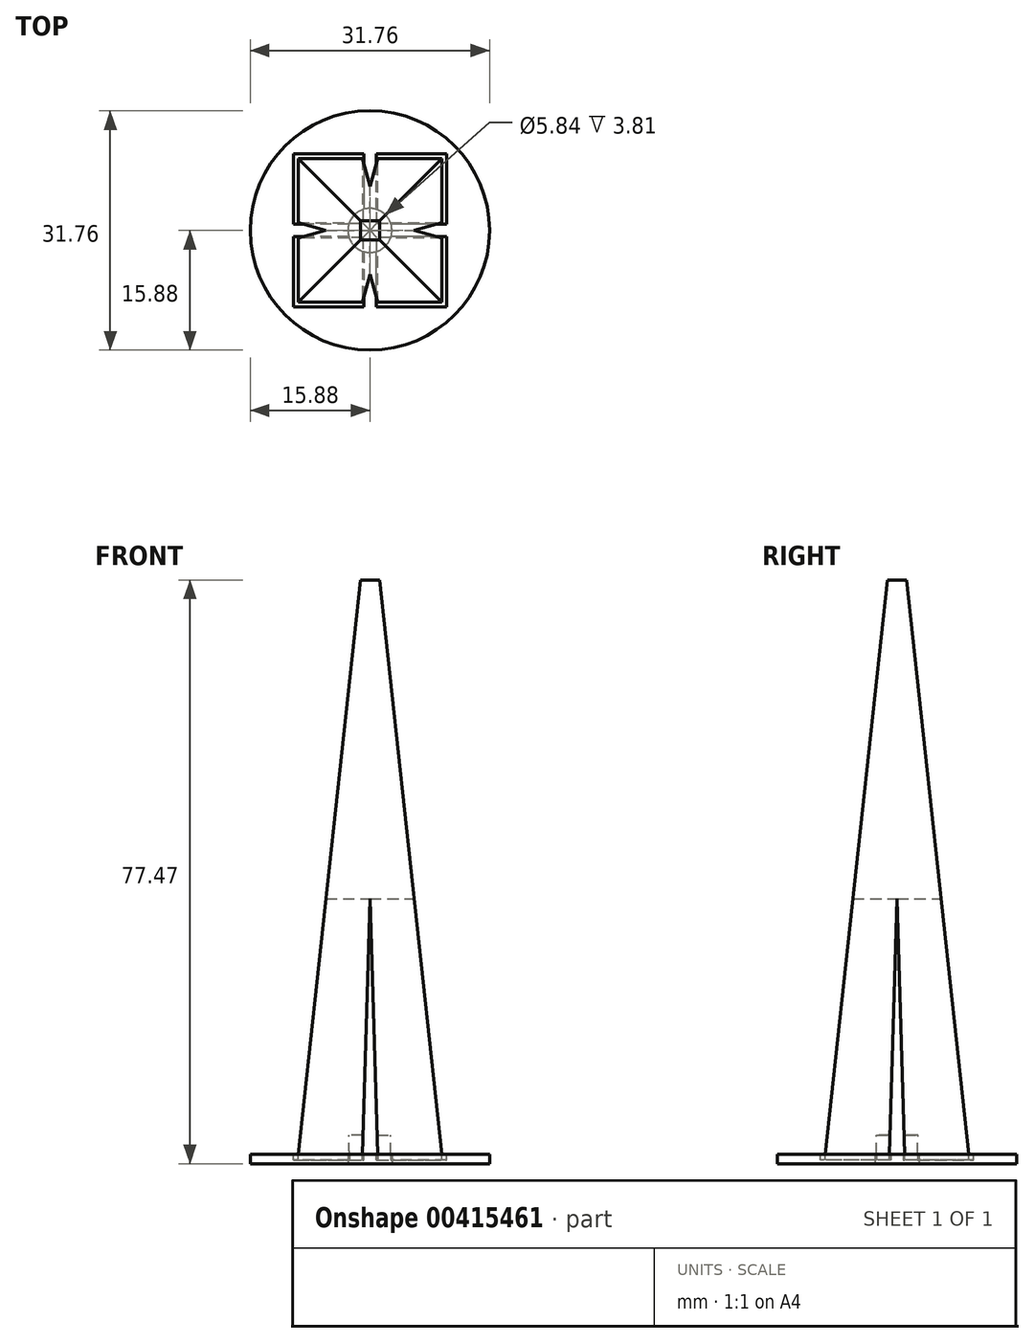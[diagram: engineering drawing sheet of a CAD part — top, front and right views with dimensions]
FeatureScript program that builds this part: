
annotation { "Feature Type Name" : "Feature", "Feature Type Description" : "" }
export const myFeature = defineFeature(function(context is Context, id is Id, definition is map)
    precondition{}
    {
        {
            var Q0;
            Q0=qCreatedBy(makeId("Top.planeOp"),FACE);
            var sketch = newSketch(context, id + "F0", { "sketchPlane" : qUnion([Q0])});
            skCircle(sketch, "E0", {"center": v(0, 0) * mm, "radius": 15.88 * mm});
            skSolve(sketch);
        }
        {
            var Q0;
            Q0=makeQuery(id+"F0.imprint","IMPRINT",FACE,{"disambiguationData":[TD([[makeQuery(id+"F0.imprint","IMPRINT",EDGE,{"derivedFrom":sQuery(id+"F0.wireOp",EDGE,"E0")}),1.0]])]});
            extrude(context, id + "F1", {"entities" : qUnion([Q0]), "oppositeDirection" : true, "depth" : 1.27 * mm});
        }
        {
            var Q0;
            Q0=qCreatedBy(makeId("Top.planeOp"),FACE);
            var sketch = newSketch(context, id + "F2", { "sketchPlane" : qUnion([Q0])});
            skLineSegment(sketch, "E1.bottom", {"start": v(-9.52, 9.53) * mm, "end": v(9.53, 9.53) * mm});
            skLineSegment(sketch, "E1.top", {"start": v(-9.53, -9.53) * mm, "end": v(9.52, -9.53) * mm});
            skLineSegment(sketch, "E1.left", {"start": v(-9.52, 9.53) * mm, "end": v(-9.53, -9.53) * mm});
            skLineSegment(sketch, "E1.right", {"start": v(9.53, 9.53) * mm, "end": v(9.52, -9.53) * mm});
            skPoint(sketch, "E1.middle", {"position": v(0, 0) * mm});
            skLineSegment(sketch, "E2", {"start": v(-1.02, 9.52) * mm, "end": v(-1.02, -9.52) * mm});
            skLineSegment(sketch, "E3", {"start": v(1.02, -9.52) * mm, "end": v(1.02, 9.52) * mm});
            skLineSegment(sketch, "E4", {"start": v(-9.52, 1.02) * mm, "end": v(9.53, 1.02) * mm});
            skLineSegment(sketch, "E5", {"start": v(9.53, -1.02) * mm, "end": v(-9.52, -1.02) * mm});
            skLineSegment(sketch, "E6", {"start": v(0, 9.53) * mm, "end": v(0, 0) * mm, "construction": true});
            skLineSegment(sketch, "E7", {"start": v(0, 0) * mm, "end": v(0, -9.53) * mm, "construction": true});
            skLineSegment(sketch, "E8", {"start": v(0, 0) * mm, "end": v(9.53, 0) * mm, "construction": true});
            skLineSegment(sketch, "E9", {"start": v(0, 0) * mm, "end": v(-9.53, 0) * mm, "construction": true});
            skSolve(sketch);
        }
        {
            var Q0;
            Q0=qCreatedBy(makeId("Top.planeOp"),FACE);
            cPlane(context, id + "F3", {"entities" : qUnion([Q0]), "cplaneType" : CPlaneType.OFFSET, "offset" : 76.2 * mm, "width" : 152.4 * mm, "height" : 152.4 * mm});
        }
        {
            var Q0;
            Q0=qCreatedBy(id+"F3.planeOp",FACE);
            var sketch = newSketch(context, id + "F4", { "sketchPlane" : qUnion([Q0])});
            skLineSegment(sketch, "E10.bottom", {"start": v(-1.27, 1.27) * mm, "end": v(1.27, 1.27) * mm});
            skLineSegment(sketch, "E10.top", {"start": v(-1.27, -1.27) * mm, "end": v(1.27, -1.27) * mm});
            skLineSegment(sketch, "E10.left", {"start": v(-1.27, 1.27) * mm, "end": v(-1.27, -1.27) * mm});
            skLineSegment(sketch, "E10.right", {"start": v(1.27, 1.27) * mm, "end": v(1.27, -1.27) * mm});
            skPoint(sketch, "E10.middle", {"position": v(0, 0) * mm});
            skSolve(sketch);
        }
        {
            var Q1;
            {var subQ0=sQuery(id+"F2.wireOp",EDGE,"E1.left");var subQ1=sQuery(id+"F2.wireOp",EDGE,"E1.bottom");var subQ2=makeQuery(id+"F2.imprint","INTERSECT",VERTEX,{"derivedFrom":[subQ1,subQ0]});Q1=makeQuery(id+"F2.imprint","IMPRINT",FACE,{"disambiguationData":[TD([[makeQuery(id+"F2.imprint","IMPRINT",EDGE,{"disambiguationData":[TD([[subQ2,-1.0]])],"derivedFrom":subQ1}),-1.0]])]});}
            var Q2;
            Q2=makeQuery(id+"F4.imprint","IMPRINT",FACE,{"disambiguationData":[TD([[makeQuery(id+"F4.imprint","IMPRINT",EDGE,{"derivedFrom":sQuery(id+"F4.wireOp",EDGE,"E10.bottom")}),-1.0]])]});
            loft(context, id + "F5", {"sheetProfilesArray" : [{ "sheetProfileEntities" : qUnion([Q1]) }, { "sheetProfileEntities" : qUnion([Q2]) }]});
        }
        {
            var Q1;
            {var subQ0=sQuery(id+"F2.wireOp",EDGE,"E1.right");var subQ1=sQuery(id+"F2.wireOp",EDGE,"E1.bottom");var subQ2=makeQuery(id+"F2.imprint","INTERSECT",VERTEX,{"derivedFrom":[subQ1,subQ0]});Q1=makeQuery(id+"F2.imprint","IMPRINT",FACE,{"disambiguationData":[TD([[makeQuery(id+"F2.imprint","IMPRINT",EDGE,{"disambiguationData":[TD([[subQ2,1.0]])],"derivedFrom":subQ1}),-1.0]])]});}
            var Q2;
            Q2=makeQuery(id+"F5.opLoft","CAP_FACE",FACE,{"disambiguationData":[OSD([makeQuery(id+"F4.imprint","IMPRINT",FACE,{"disambiguationData":[TD([[makeQuery(id+"F4.imprint","IMPRINT",EDGE,{"derivedFrom":sQuery(id+"F4.wireOp",EDGE,"E10.bottom")}),-1.0]])]})])],"isStart":true});
            loft(context, id + "F6", {"operationType" : NewBodyOperationType.ADD, "sheetProfilesArray" : [{ "sheetProfileEntities" : qUnion([Q1]) }, { "sheetProfileEntities" : qUnion([Q2]) }]});
        }
        {
            var Q1;
            {var subQ0=sQuery(id+"F2.wireOp",EDGE,"E1.left");var subQ1=sQuery(id+"F2.wireOp",EDGE,"E1.top");var subQ2=makeQuery(id+"F2.imprint","INTERSECT",VERTEX,{"derivedFrom":[subQ1,subQ0]});Q1=makeQuery(id+"F2.imprint","IMPRINT",FACE,{"disambiguationData":[TD([[makeQuery(id+"F2.imprint","IMPRINT",EDGE,{"disambiguationData":[TD([[subQ2,-1.0]])],"derivedFrom":subQ1}),1.0]])]});}
            var Q2;
            Q2=makeQuery(id+"F5.opLoft","CAP_FACE",FACE,{"disambiguationData":[OSD([makeQuery(id+"F4.imprint","IMPRINT",FACE,{"disambiguationData":[TD([[makeQuery(id+"F4.imprint","IMPRINT",EDGE,{"derivedFrom":sQuery(id+"F4.wireOp",EDGE,"E10.bottom")}),-1.0]])]})])],"isStart":true});
            loft(context, id + "F7", {"operationType" : NewBodyOperationType.ADD, "sheetProfilesArray" : [{ "sheetProfileEntities" : qUnion([Q1]) }, { "sheetProfileEntities" : qUnion([Q2]) }]});
        }
        {
            var Q1;
            {var subQ0=sQuery(id+"F2.wireOp",EDGE,"E1.right");var subQ1=sQuery(id+"F2.wireOp",EDGE,"E1.top");var subQ2=makeQuery(id+"F2.imprint","INTERSECT",VERTEX,{"derivedFrom":[subQ1,subQ0]});Q1=makeQuery(id+"F2.imprint","IMPRINT",FACE,{"disambiguationData":[TD([[makeQuery(id+"F2.imprint","IMPRINT",EDGE,{"disambiguationData":[TD([[subQ2,1.0]])],"derivedFrom":subQ1}),1.0]])]});}
            var Q2;
            Q2=makeQuery(id+"F5.opLoft","CAP_FACE",FACE,{"disambiguationData":[OSD([makeQuery(id+"F4.imprint","IMPRINT",FACE,{"disambiguationData":[TD([[makeQuery(id+"F4.imprint","IMPRINT",EDGE,{"derivedFrom":sQuery(id+"F4.wireOp",EDGE,"E10.bottom")}),-1.0]])]})])],"isStart":true});
            loft(context, id + "F8", {"operationType" : NewBodyOperationType.ADD, "sheetProfilesArray" : [{ "sheetProfileEntities" : qUnion([Q1]) }, { "sheetProfileEntities" : qUnion([Q2]) }]});
        }
        {
            var Q0;
            Q0=makeQuery(id+"F1.opExtrude","CAP_FACE",FACE,{"disambiguationData":[OSD([sQuery(id+"F0.wireOp",EDGE,"E0")])],"isStart":true});
            var sketch = newSketch(context, id + "F9", { "sketchPlane" : qUnion([Q0])});
            skLineSegment(sketch, "E11", {"start": v(0, 0) * mm, "end": v(0, 15.88) * mm, "construction": true});
            skLineSegment(sketch, "E12", {"start": v(0, 0) * mm, "end": v(15.88, 0) * mm, "construction": true});
            skLineSegment(sketch, "E13.bottom", {"start": v(-10.16, 10.16) * mm, "end": v(10.16, 10.16) * mm});
            skLineSegment(sketch, "E13.top", {"start": v(-10.16, -10.16) * mm, "end": v(10.16, -10.16) * mm});
            skLineSegment(sketch, "E13.left", {"start": v(-10.16, 10.16) * mm, "end": v(-10.16, -10.16) * mm});
            skLineSegment(sketch, "E13.right", {"start": v(10.16, 10.16) * mm, "end": v(10.16, -10.16) * mm});
            skPoint(sketch, "E13.middle", {"position": v(0, 0) * mm});
            skLineSegment(sketch, "E14", {"start": v(-0.83, 15.85) * mm, "end": v(-0.83, -15.85) * mm});
            skLineSegment(sketch, "E15", {"start": v(0.83, -15.85) * mm, "end": v(0.83, 15.85) * mm});
            skLineSegment(sketch, "E16", {"start": v(15.85, 0.83) * mm, "end": v(-15.85, 0.83) * mm});
            skLineSegment(sketch, "E17", {"start": v(15.85, -0.83) * mm, "end": v(-15.85, -0.83) * mm});
            skSolve(sketch);
        }
        {
            var Q0;
            {var subQ0=sQuery(id+"F9.wireOp",EDGE,"E13.right");var subQ1=sQuery(id+"F9.wireOp",EDGE,"E13.bottom");var subQ2=makeQuery(id+"F9.imprint","INTERSECT",VERTEX,{"derivedFrom":[subQ1,subQ0]});Q0=makeQuery(id+"F9.imprint","IMPRINT",FACE,{"disambiguationData":[TD([[makeQuery(id+"F9.imprint","IMPRINT",EDGE,{"disambiguationData":[TD([[subQ2,1.0]])],"derivedFrom":subQ1}),-1.0]])]});}
            var Q1;
            {var subQ0=sQuery(id+"F9.wireOp",EDGE,"E13.left");var subQ1=sQuery(id+"F9.wireOp",EDGE,"E13.bottom");var subQ2=makeQuery(id+"F9.imprint","INTERSECT",VERTEX,{"derivedFrom":[subQ1,subQ0]});Q1=makeQuery(id+"F9.imprint","IMPRINT",FACE,{"disambiguationData":[TD([[makeQuery(id+"F9.imprint","IMPRINT",EDGE,{"disambiguationData":[TD([[subQ2,-1.0]])],"derivedFrom":subQ1}),-1.0]])]});}
            var Q2;
            {var subQ0=sQuery(id+"F9.wireOp",EDGE,"E13.right");var subQ1=sQuery(id+"F9.wireOp",EDGE,"E13.top");var subQ2=makeQuery(id+"F9.imprint","INTERSECT",VERTEX,{"derivedFrom":[subQ1,subQ0]});Q2=makeQuery(id+"F9.imprint","IMPRINT",FACE,{"disambiguationData":[TD([[makeQuery(id+"F9.imprint","IMPRINT",EDGE,{"disambiguationData":[TD([[subQ2,1.0]])],"derivedFrom":subQ1}),1.0]])]});}
            var Q3;
            {var subQ0=sQuery(id+"F9.wireOp",EDGE,"E13.left");var subQ1=sQuery(id+"F9.wireOp",EDGE,"E13.top");var subQ2=makeQuery(id+"F9.imprint","INTERSECT",VERTEX,{"derivedFrom":[subQ1,subQ0]});Q3=makeQuery(id+"F9.imprint","IMPRINT",FACE,{"disambiguationData":[TD([[makeQuery(id+"F9.imprint","IMPRINT",EDGE,{"disambiguationData":[TD([[subQ2,-1.0]])],"derivedFrom":subQ1}),1.0]])]});}
            extrude(context, id + "F10", {"entities" : qUnion([Q0, Q1, Q2, Q3]), "operationType" : NewBodyOperationType.REMOVE, "oppositeDirection" : true, "depth" : 0.76 * mm});
        }
        {
            var Q0;
            Q0=makeQuery(id+"F1.opExtrude","CAP_FACE",FACE,{"disambiguationData":[OSD([sQuery(id+"F0.wireOp",EDGE,"E0")])],"isStart":false});
            var sketch = newSketch(context, id + "F11", { "sketchPlane" : qUnion([Q0])});
            skCircle(sketch, "E18", {"center": v(0, 0) * mm, "radius": 2.92 * mm});
            skSolve(sketch);
        }
        {
            var Q0;
            Q0=makeQuery(id+"F11.imprint","IMPRINT",FACE,{"disambiguationData":[TD([[makeQuery(id+"F11.imprint","IMPRINT",EDGE,{"derivedFrom":sQuery(id+"F11.wireOp",EDGE,"E18")}),1.0]])]});
            extrude(context, id + "F12", {"entities" : qUnion([Q0]), "operationType" : NewBodyOperationType.REMOVE, "oppositeDirection" : true, "depth" : 3.8 * mm});
        }
    });
